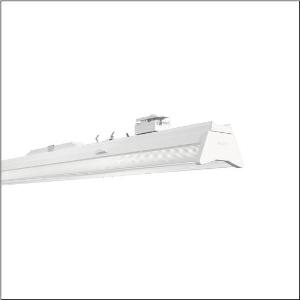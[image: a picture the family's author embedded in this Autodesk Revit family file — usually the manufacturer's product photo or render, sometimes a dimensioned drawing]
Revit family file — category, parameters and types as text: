
# Revit family: licross_r__21_performance_mo_52ts16dnd75f_76b1
name_source: partatom
category: Lighting Fixtures
units: mm (PartAtom-declared; Revit-internal decimal feet)

## family parameters
Cut with Voids When Loaded = No
Host = Face
Light Source = No
Part Type = Normal
Room Calculation Point = No
Round Connector Dimension = Use Diameter
Shared = No

## types (1)
- --- (1 x LED, 7810 lm, 60.9 W, 4000K)
    Apparent Load = 61 VA
    CIE Flux Codes = 66 88 96 79 100
    Color Rendering = 90
    Color Temperature = 4000K
    Default Elevation = 1800 mm
    Description = Licross® 21 Performance MO, luminaire insert, of sheet steel, galvanised, coil coated, white, length: 1.500mm, width: 120mm, height: 123mm, LED rated luminous flux: 7.810lm, light colour: 940, control gear: DALI 2, control gear: ECG DALI, with plug, 5-pole, with phase selection, mains connection: 220..240V, AC, 50/60Hz, rated input power: 61W, halogen-free wiring, primary light control with lens, of plastic, primary optical cover: cover, of PMMA, light emission: direct/indirect distribution, primary light characteristic: symmetric, protection rating (complete): IP50, insulation class (complete): insulation class I (protective earthing), certification: CE, ENEC, VDE, UKCA, protection symbol: D if used in an environment with non-conductive dust loads with corresponding accessories, impact resistance: IK06, permissible ambient temperature for indoor applications: -25..+40°C, corresponds to IFS (International Featured Standards) requirements for safety and quality in the food industry, reducing of maximum allowable ambient temperature of 5°C with ceiling mounting, LABS conformity tested according to VDMA 24364:2018-05, packaging unit: 1 piece
    Height = 114 mm
    Lamp = 1 x LED
    Lamp Light Flux = 7810 lm
    Lamp Power = 60.9 W
    Lamp count = 1
    Length = 1500 mm
    Luminous efficacy = 128 lm/W
    Manufacturer = Siteco
    ModVariant = No
    Model = 52TS16DND75F
    Mounting Place = Ceiling
    Mounting Type = Pendant
    Number of Poles = 1
    OnlyDefault = Yes
    Power Factor = 1
    Product Name = Licross® 21 Performance MO
    Product group = luminaire insert
    ProductGroupID = 901
    Protection Class = Protection class I
    Protection Degree = IP 50
    RLX_Detail_Level = 1
    RLX_Emergency_Light_Flux = 0 lm
    RLX_Emergency_Type = 0
    RLX_Emergency_Type_DB = No
    RlxData = <blob elided: 33985 chars, md5=f83aa37b>
    Socket = socket
    Standby Power = 0 W
    System Light Flux = 7810 lm
    System Power = 61 W
    Type Comments = factory setting: luminous flux: 100 % | dim-lin: 254 | 405 mA
    Type Image = l_1256138.jpg
    URL = http://relux.com
    VarID = @adj_136653
    Voltage = 0 V
    Weight = 0.00 kg
    Width = 120 mm

## geometry (parser evidence)
native form markers: Blend x4, Sweep x9
no freeform markers — native parametric forms only
